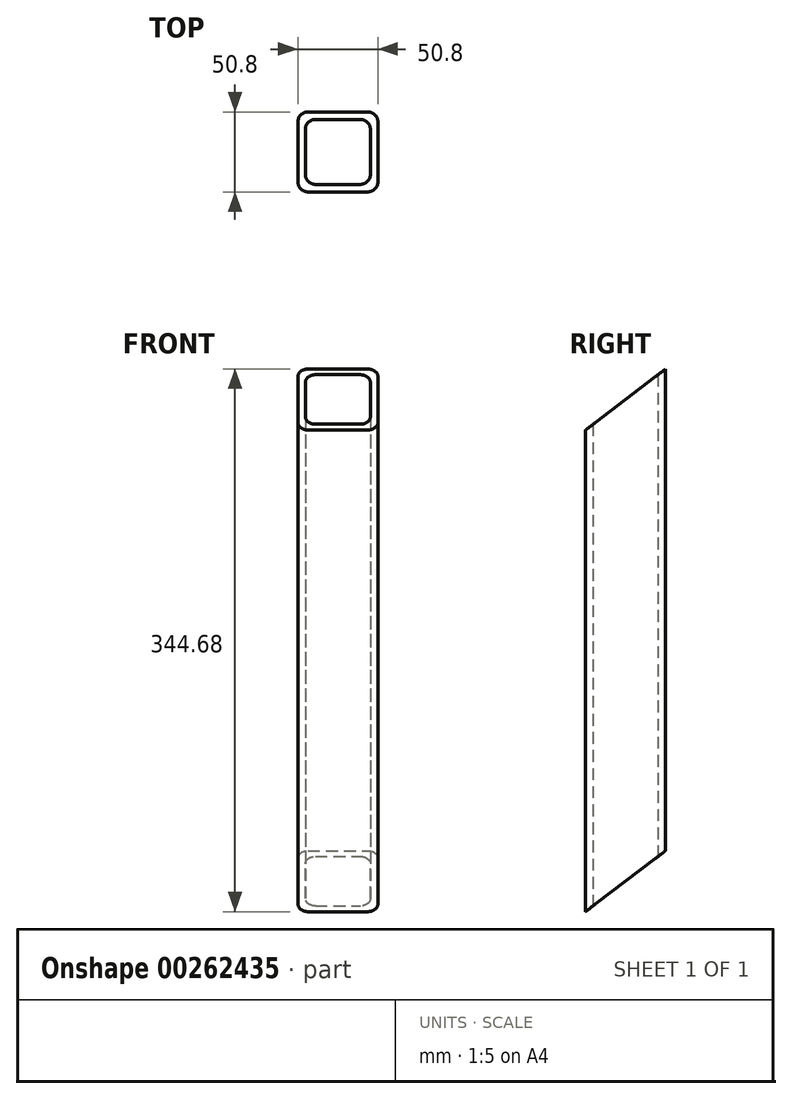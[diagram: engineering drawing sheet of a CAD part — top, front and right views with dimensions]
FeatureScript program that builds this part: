
annotation { "Feature Type Name" : "Feature", "Feature Type Description" : "" }
export const myFeature = defineFeature(function(context is Context, id is Id, definition is map)
    precondition{}
    {
        {
            var Q0;
            Q0=qCreatedBy(makeId("Top.planeOp"),FACE);
            var sketch = newSketch(context, id + "F0", { "sketchPlane" : qUnion([Q0])});
            skLineSegment(sketch, "E0.bottom", {"start": v(14.29, 20.64) * mm, "end": v(-14.29, 20.64) * mm});
            skLineSegment(sketch, "E0.top", {"start": v(14.29, -20.64) * mm, "end": v(-14.29, -20.64) * mm});
            skLineSegment(sketch, "E0.left", {"start": v(20.64, 14.29) * mm, "end": v(20.64, -14.29) * mm});
            skLineSegment(sketch, "E0.right", {"start": v(-20.64, 14.29) * mm, "end": v(-20.64, -14.29) * mm});
            skPoint(sketch, "E0.middle", {"position": v(0, 0) * mm});
            skLineSegment(sketch, "E1.bottom", {"start": v(19.05, 25.4) * mm, "end": v(-19.05, 25.4) * mm});
            skLineSegment(sketch, "E1.top", {"start": v(19.05, -25.4) * mm, "end": v(-19.05, -25.4) * mm});
            skLineSegment(sketch, "E1.left", {"start": v(25.4, 19.05) * mm, "end": v(25.4, -19.05) * mm});
            skLineSegment(sketch, "E1.right", {"start": v(-25.4, 19.05) * mm, "end": v(-25.4, -19.05) * mm});
            skPoint(sketch, "E2.visualSharp", {"position": v(-25.4, 25.4) * mm});
            skArc(sketch, "E2.filletArc", {"start": v(-19.05, 25.4) * mm, "mid": v(-23.54, 23.54) * mm, "end": v(-25.4, 19.05) * mm});
            skPoint(sketch, "E3.visualSharp", {"position": v(-20.64, 20.64) * mm});
            skArc(sketch, "E3.filletArc", {"start": v(-14.29, 20.64) * mm, "mid": v(-18.78, 18.78) * mm, "end": v(-20.64, 14.29) * mm});
            skPoint(sketch, "E4.visualSharp", {"position": v(20.64, 20.64) * mm});
            skArc(sketch, "E4.filletArc", {"start": v(20.64, 14.29) * mm, "mid": v(18.78, 18.78) * mm, "end": v(14.29, 20.64) * mm});
            skPoint(sketch, "E5.visualSharp", {"position": v(25.4, 25.4) * mm});
            skArc(sketch, "E5.filletArc", {"start": v(25.4, 19.05) * mm, "mid": v(23.54, 23.54) * mm, "end": v(19.05, 25.4) * mm});
            skPoint(sketch, "E6.visualSharp", {"position": v(-25.4, -25.4) * mm});
            skArc(sketch, "E6.filletArc", {"start": v(-25.4, -19.05) * mm, "mid": v(-23.54, -23.54) * mm, "end": v(-19.05, -25.4) * mm});
            skPoint(sketch, "E7.visualSharp", {"position": v(-20.64, -20.64) * mm});
            skArc(sketch, "E7.filletArc", {"start": v(-20.64, -14.29) * mm, "mid": v(-18.78, -18.78) * mm, "end": v(-14.29, -20.64) * mm});
            skPoint(sketch, "E8.visualSharp", {"position": v(20.64, -20.64) * mm});
            skArc(sketch, "E8.filletArc", {"start": v(14.29, -20.64) * mm, "mid": v(18.78, -18.78) * mm, "end": v(20.64, -14.29) * mm});
            skPoint(sketch, "E9.visualSharp", {"position": v(25.4, -25.4) * mm});
            skArc(sketch, "E9.filletArc", {"start": v(19.05, -25.4) * mm, "mid": v(23.54, -23.54) * mm, "end": v(25.4, -19.05) * mm});
            skSolve(sketch);
        }
        {
            var Q0;
            Q0 = qSketchRegion(id + "F0", true);
            extrude(context, id + "F1", {"entities" : qUnion([Q0]), "depth" : 344.68 * mm});
        }
        {
            var Q0;
            Q0=qCreatedBy(makeId("Right.planeOp"),FACE);
            var sketch = newSketch(context, id + "F2", { "sketchPlane" : qUnion([Q0])});
            skLineSegment(sketch, "E10.top", {"start": v(25.4, 0) * mm, "end": v(-25.4, 0) * mm});
            skLineSegment(sketch, "E10.left", {"start": v(25.4, 38.7) * mm, "end": v(25.4, 0) * mm});
            skPoint(sketch, "E10.middle", {"position": v(0, 19.35) * mm});
            skLineSegment(sketch, "E11.bottom", {"start": v(25.4, 344.68) * mm, "end": v(-25.4, 344.68) * mm});
            skLineSegment(sketch, "E11.right", {"start": v(-25.4, 344.68) * mm, "end": v(-25.4, 305.98) * mm});
            skPoint(sketch, "E11.middle", {"position": v(0, 325.33) * mm});
            skLineSegment(sketch, "E12", {"start": v(-25.4, 0) * mm, "end": v(25.4, 38.7) * mm});
            skLineSegment(sketch, "E13", {"start": v(-25.4, 305.98) * mm, "end": v(25.4, 344.68) * mm});
            skPoint(sketch, "E11.left.end.orphan", {"position": v(25.4, 305.98) * mm});
            skPoint(sketch, "E10.right.start.orphan", {"position": v(-25.4, 38.7) * mm});
            skSolve(sketch);
        }
        {
            var Q0;
            Q0 = qSketchRegion(id + "F2", true);
            extrude(context, id + "F3", {"entities" : qUnion([Q0]), "operationType" : NewBodyOperationType.REMOVE, "endBound" : BoundingType.THROUGH_ALL, "oppositeDirection" : true, "depth" : 25.4 * mm, "hasSecondDirection" : true, "secondDirectionBound" : SecondDirectionBoundingType.THROUGH_ALL, "secondDirectionOppositeDirection" : false, "secondDirectionDepth" : 25.4 * mm});
        }
    });
